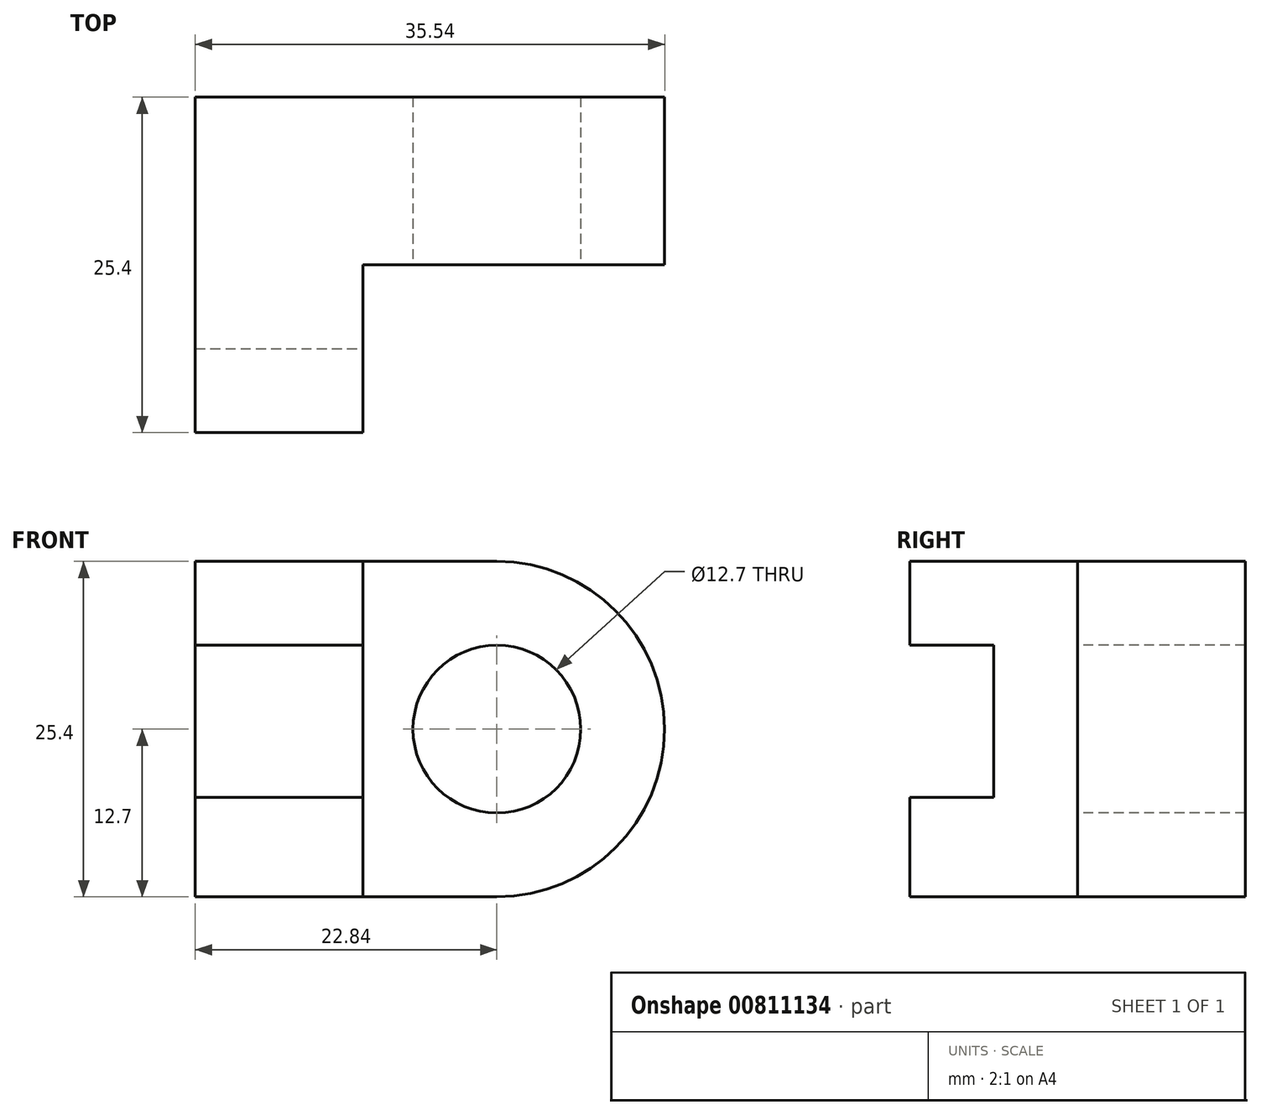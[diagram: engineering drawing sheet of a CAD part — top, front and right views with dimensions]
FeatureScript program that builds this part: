
annotation { "Feature Type Name" : "Feature", "Feature Type Description" : "" }
export const myFeature = defineFeature(function(context is Context, id is Id, definition is map)
    precondition{}
    {
        {
            var Q0;
            Q0=qCreatedBy(makeId("Front.planeOp"),FACE);
            var sketch = newSketch(context, id + "F0", { "sketchPlane" : qUnion([Q0])});
            skLineSegment(sketch, "E0", {"start": v(0, 0) * mm, "end": v(0, 25.4) * mm});
            skLineSegment(sketch, "E1", {"start": v(0, 25.4) * mm, "end": v(44.45, 25.4) * mm});
            skLineSegment(sketch, "E2", {"start": v(44.45, 25.4) * mm, "end": v(44.45, 0) * mm});
            skLineSegment(sketch, "E3", {"start": v(44.45, 0) * mm, "end": v(0, 0) * mm});
            skSolve(sketch);
        }
        {
            var Q0;
            Q0 = qSketchRegion(id + "F0", true);
            extrude(context, id + "F1", {"entities" : qUnion([Q0]), "depth" : 25.4 * mm, "offsetDistance" : 25.4 * mm});
        }
        {
            var Q0;
            Q0=makeQuery(id+"F1.opExtrude","CAP_FACE",FACE,{"disambiguationData":[OSD([sQuery(id+"F0.wireOp",EDGE,"E0"),sQuery(id+"F0.wireOp",EDGE,"E1"),sQuery(id+"F0.wireOp",EDGE,"E2"),sQuery(id+"F0.wireOp",EDGE,"E3")])],"isStart":false});
            var sketch = newSketch(context, id + "F2", { "sketchPlane" : qUnion([Q0])});
            skLineSegment(sketch, "E4", {"start": v(0, 0) * mm, "end": v(12.7, 0) * mm});
            skLineSegment(sketch, "E5", {"start": v(12.7, 0) * mm, "end": v(12.7, 25.4) * mm});
            skLineSegment(sketch, "E6", {"start": v(12.7, 25.4) * mm, "end": v(0, 25.4) * mm});
            skLineSegment(sketch, "E7", {"start": v(0, 25.4) * mm, "end": v(0, 0) * mm});
            skSolve(sketch);
        }
        {
            var Q0;
            {var subQ0=sQuery(id+"F2.wireOp",EDGE,"E5");Q0=makeQuery(id+"F2.imprint","IMPRINT",FACE,{"disambiguationData":[TD([[makeQuery(id+"F2.imprint","IMPRINT",EDGE,{"derivedFrom":subQ0}),-1.0]])]});}
            extrude(context, id + "F3", {"entities" : qUnion([Q0]), "operationType" : NewBodyOperationType.REMOVE, "oppositeDirection" : true, "depth" : 12.7 * mm, "offsetDistance" : 25.4 * mm});
        }
        {
            var Q0;
            Q0=makeQuery(id+"F1.opExtrude","CAP_FACE",FACE,{"disambiguationData":[OSD([sQuery(id+"F0.wireOp",EDGE,"E0"),sQuery(id+"F0.wireOp",EDGE,"E1"),sQuery(id+"F0.wireOp",EDGE,"E2"),sQuery(id+"F0.wireOp",EDGE,"E3")])],"isStart":false});
            var sketch = newSketch(context, id + "F4", { "sketchPlane" : qUnion([Q0])});
            skLineSegment(sketch, "E8", {"start": v(0, 0) * mm, "end": v(0, 7.54) * mm});
            skLineSegment(sketch, "E9", {"start": v(0, 7.54) * mm, "end": v(12.7, 7.54) * mm});
            skLineSegment(sketch, "E10", {"start": v(12.7, 7.54) * mm, "end": v(12.63, -1) * mm});
            skLineSegment(sketch, "E11", {"start": v(0, 25.4) * mm, "end": v(0, 19.05) * mm});
            skLineSegment(sketch, "E12", {"start": v(0, 19.05) * mm, "end": v(12.7, 19.05) * mm});
            skLineSegment(sketch, "E13", {"start": v(12.7, 19.05) * mm, "end": v(12.7, 25.4) * mm});
            skSolve(sketch);
        }
        {
            var Q0;
            {var subQ0=sQuery(id+"F4.wireOp",EDGE,"E9");Q0=makeQuery(id+"F4.imprint","IMPRINT",FACE,{"disambiguationData":[TD([[makeQuery(id+"F4.imprint","IMPRINT",EDGE,{"derivedFrom":subQ0}),1.0]])]});}
            extrude(context, id + "F5", {"entities" : qUnion([Q0]), "operationType" : NewBodyOperationType.REMOVE, "oppositeDirection" : true, "depth" : 6.35 * mm, "offsetDistance" : 25.4 * mm});
        }
        {
            var Q0;
            Q0=makeQuery(id+"F3.boolean.opBoolean","COPY",FACE,{"derivedFrom":makeQuery(id+"F3.opExtrude","CAP_FACE",FACE,{"disambiguationData":[OSD([sQuery(id+"F0.wireOp",EDGE,"E1"),sQuery(id+"F0.wireOp",EDGE,"E2"),sQuery(id+"F0.wireOp",EDGE,"E3"),sQuery(id+"F2.wireOp",EDGE,"E5")])],"isStart":false})});
            var sketch = newSketch(context, id + "F6", { "sketchPlane" : qUnion([Q0])});
            skLineSegment(sketch, "E14", {"start": v(12.7, 25.4) * mm, "end": v(22.84, 25.4) * mm});
            skLineSegment(sketch, "E15", {"start": v(22.84, 25.4) * mm, "end": v(22.84, 0) * mm});
            skLineSegment(sketch, "E16", {"start": v(22.84, 0) * mm, "end": v(12.7, 0) * mm});
            skArc(sketch, "E17", {"start": v(22.84, 0) * mm, "mid": v(35.54, 12.7) * mm, "end": v(22.84, 25.4) * mm});
            skSolve(sketch);
        }
        {
            var Q0;
            {var subQ0=sQuery(id+"F6.wireOp",EDGE,"E17");Q0=makeQuery(id+"F6.imprint","IMPRINT",FACE,{"disambiguationData":[TD([[makeQuery(id+"F6.imprint","IMPRINT",EDGE,{"derivedFrom":subQ0}),-1.0]])]});}
            extrude(context, id + "F7", {"entities" : qUnion([Q0]), "operationType" : NewBodyOperationType.REMOVE, "endBound" : BoundingType.UP_TO_NEXT, "oppositeDirection" : true, "depth" : 25.4 * mm, "offsetDistance" : 25.4 * mm});
        }
        {
            var Q0;
            Q0=makeQuery(id+"F3.boolean.opBoolean","COPY",FACE,{"derivedFrom":makeQuery(id+"F3.opExtrude","CAP_FACE",FACE,{"disambiguationData":[OSD([sQuery(id+"F0.wireOp",EDGE,"E1"),sQuery(id+"F0.wireOp",EDGE,"E2"),sQuery(id+"F0.wireOp",EDGE,"E3"),sQuery(id+"F2.wireOp",EDGE,"E5")])],"isStart":false})});
            var sketch = newSketch(context, id + "F8", { "sketchPlane" : qUnion([Q0])});
            skLineSegment(sketch, "E18", {"start": v(22.84, 25.4) * mm, "end": v(22.84, 12.7) * mm});
            skLineSegment(sketch, "E19", {"start": v(22.84, 12.7) * mm, "end": v(22.84, 0) * mm});
            skSolve(sketch);
        }
        {
            var Q0;
            Q0=sQuery(id+"F8.wireOp",VERTEX,"E18.end");
            var Q1;
            Q1=makeQuery(id+"F1.opExtrude","SWEPT_BODY",BODY,{"disambiguationData":[OSD([sQuery(id+"F0.wireOp",EDGE,"E0"),sQuery(id+"F0.wireOp",EDGE,"E1"),sQuery(id+"F0.wireOp",EDGE,"E2"),sQuery(id+"F0.wireOp",EDGE,"E3")])]});
            hole(context, id + "F9", {"style" : HoleStyle.SIMPLE, "endStyle" : HoleEndStyle.THROUGH, "holeDiameter" : 12.7 * mm, "majorDiameter" : 6.35 * mm, "isTappedThrough" : true, "tappedDepth" : 12.7 * mm, "tapClearance" : 3, "locations" : qUnion([Q0]), "scope" : qUnion([Q1])});
        }
    });
